# Revit family: Haworth_XSeries_ComboValet_42WideMultiDrawers
name_source: partatom
category: Furniture Systems
units: mm (PartAtom-declared; Revit-internal decimal feet)

## family parameters
Always vertical = Yes
Cut with Voids When Loaded = No
OmniClass Number = 23.40.70.14.64.21
OmniClass Title = Systems Furniture
Part Type = Normal
Room Calculation Point = No
Round Connector Dimension = Use Diameter
Shared = No
Work Plane-Based = No

## types (1)
- 18d 42w 63h - Valet Storage File Box Box Lat Lat
    Actual Depth = 18 3/4"
    Actual Height = 63 1/2"
    Actual Width = 41 7/8"
    Assembly Code = E2020200
    Cabinet Height = 39 1/2"
    Classic Pull = No
    Crescent Pull = No
    Description = Haworth XSeries Combo Unit Valet - 18d 42w 63h - File Box Box Lat Lat
    Door Height = 60 1/8"
    Door Height 2 = 23 3/4"
    Door Width = 11 7/8"
    Drawer 1 Height = 12"
    Drawer 2 Height = 12"
    Drawer 3 Height = 12"
    Drawer 4 Height = 5 15/16"
    Drawer Width = 29 7/8"
    Ellipse Pull = No
    J Pull = No
    Linear Pull = Yes
    Manufacturer = Haworth
    Max. Height = 63 1/2"
    Max. Width = 47 7/8"
    Min. Height = 27 1/2"
    Min. Width = 29 7/8"
    Model = JVPP-0542
    Pull Finish = Haworth _ Metal _ Brushed Aluminum
    Pull Height Centerline = 48 1/4"
    Pull Height Centerline 2 = 11 7/8"
    Radius Pull = No
    Revision Number = 4
    Shelf Depth = 28 1/2"
    Shelf Width = 17 1/4"
    Size = Verify Final Dim. w/ Haworth
    Sustainability Info = https://www.haworth.com
    Taper Pull = No
    Top Height = 24"
    Touch Latch = No
    URL = http://www.haworth.com
    URL - Product = https://www.haworth.com
    Warranty = https://cdn.shopify.com

## geometry (parser evidence)
native form markers: Sweep x10
no freeform markers — native parametric forms only
